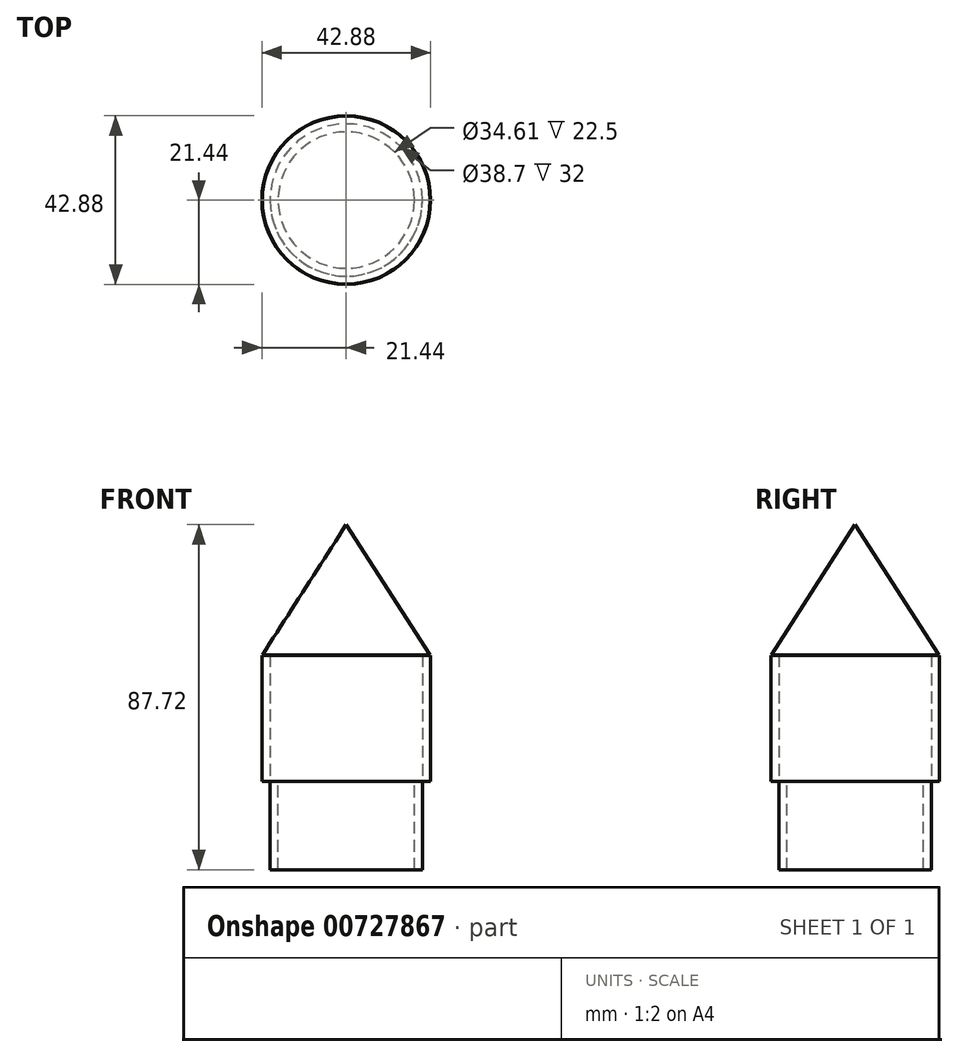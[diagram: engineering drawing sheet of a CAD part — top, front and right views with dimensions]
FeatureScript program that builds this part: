
annotation { "Feature Type Name" : "Feature", "Feature Type Description" : "" }
export const myFeature = defineFeature(function(context is Context, id is Id, definition is map)
    precondition{}
    {
        {
            var Q0;
            Q0=qCreatedBy(makeId("Top.planeOp"),FACE);
            var sketch = newSketch(context, id + "F0", { "sketchPlane" : qUnion([Q0])});
            skCircle(sketch, "E0", {"center": v(0, 0) * mm, "radius": 21.43 * mm});
            skSolve(sketch);
        }
        {
            var Q0;
            Q0=makeQuery(id+"F0.imprint","IMPRINT",FACE,{"disambiguationData":[TD([[makeQuery(id+"F0.imprint","IMPRINT",EDGE,{"derivedFrom":sQuery(id+"F0.wireOp",EDGE,"E0")}),1.0]])]});
            extrude(context, id + "F1", {"entities" : qUnion([Q0]), "depth" : 32 * mm, "offsetDistance" : 25 * mm});
        }
        {
            var Q0;
            Q0=qCreatedBy(makeId("Top.planeOp"),FACE);
            var sketch = newSketch(context, id + "F2", { "sketchPlane" : qUnion([Q0])});
            skCircle(sketch, "E1", {"center": v(0, 0) * mm, "radius": 19.35 * mm});
            skSolve(sketch);
        }
        {
            var Q0;
            Q0=sQuery(id+"F2.wireOp",VERTEX,"E1.center");
            var Q1;
            Q1=makeQuery(id+"F1.opExtrude","SWEPT_BODY",BODY,{"disambiguationData":[OSD([sQuery(id+"F0.wireOp",EDGE,"E0")])]});
            hole(context, id + "F3", {"style" : HoleStyle.SIMPLE, "endStyle" : HoleEndStyle.THROUGH, "oppositeDirection" : true, "holeDiameter" : 38.7 * mm, "majorDiameter" : 5 * mm, "isTappedThrough" : true, "tappedDepth" : 12 * mm, "tapClearance" : 3, "locations" : qUnion([Q0]), "scope" : qUnion([Q1])});
        }
        {
            var Q0;
            Q0=qCreatedBy(makeId("Front.planeOp"),FACE);
            var sketch = newSketch(context, id + "F4", { "sketchPlane" : qUnion([Q0])});
            skLineSegment(sketch, "E2", {"start": v(0, 0) * mm, "end": v(0, 32.6) * mm});
            skSolve(sketch);
        }
        {
            var Q0;
            Q0=qCreatedBy(makeId("Right.planeOp"),FACE);
            var sketch = newSketch(context, id + "F5", { "sketchPlane" : qUnion([Q0])});
            skLineSegment(sketch, "E3", {"start": v(0, 32.34) * mm, "end": v(0, 65.22) * mm});
            skLineSegment(sketch, "E4", {"start": v(0, 65.22) * mm, "end": v(-21.32, 32.07) * mm});
            skLineSegment(sketch, "E5", {"start": v(-21.32, 32.07) * mm, "end": v(0, 32.07) * mm});
            skLineSegment(sketch, "E6", {"start": v(0, 32.07) * mm, "end": v(0, 32.34) * mm});
            skSolve(sketch);
        }
        {
            var Q0;
            Q0=makeQuery(id+"F5.imprint","IMPRINT",FACE,{"disambiguationData":[TD([[makeQuery(id+"F5.imprint","IMPRINT",EDGE,{"derivedFrom":sQuery(id+"F5.wireOp",EDGE,"E3")}),1.0]])]});
            var Q1;
            Q1=sQuery(id+"F4.wireOp",EDGE,"E2");
            revolve(context, id + "F6", {"surfaceOperationType" : NewSurfaceOperationType.NEW, "entities" : qUnion([Q0]), "axis" : qUnion([Q1]), "revolveType" : RevolveType.FULL});
        }
        {
            var Q0;
            Q0=qCreatedBy(makeId("Top.planeOp"),FACE);
            var sketch = newSketch(context, id + "F7", { "sketchPlane" : qUnion([Q0])});
            skCircle(sketch, "E7", {"center": v(0, 0) * mm, "radius": 19.35 * mm});
            skCircle(sketch, "E8", {"center": v(0, 0) * mm, "radius": 17.3 * mm});
            skSolve(sketch);
        }
        {
            var Q0;
            Q0=makeQuery(id+"F7.imprint","IMPRINT",FACE,{"disambiguationData":[TD([[makeQuery(id+"F7.imprint","IMPRINT",EDGE,{"derivedFrom":sQuery(id+"F7.wireOp",EDGE,"E7")}),1.0]])]});
            extrude(context, id + "F8", {"entities" : qUnion([Q0]), "oppositeDirection" : true, "depth" : 22.5 * mm, "offsetDistance" : 25 * mm});
        }
    });
